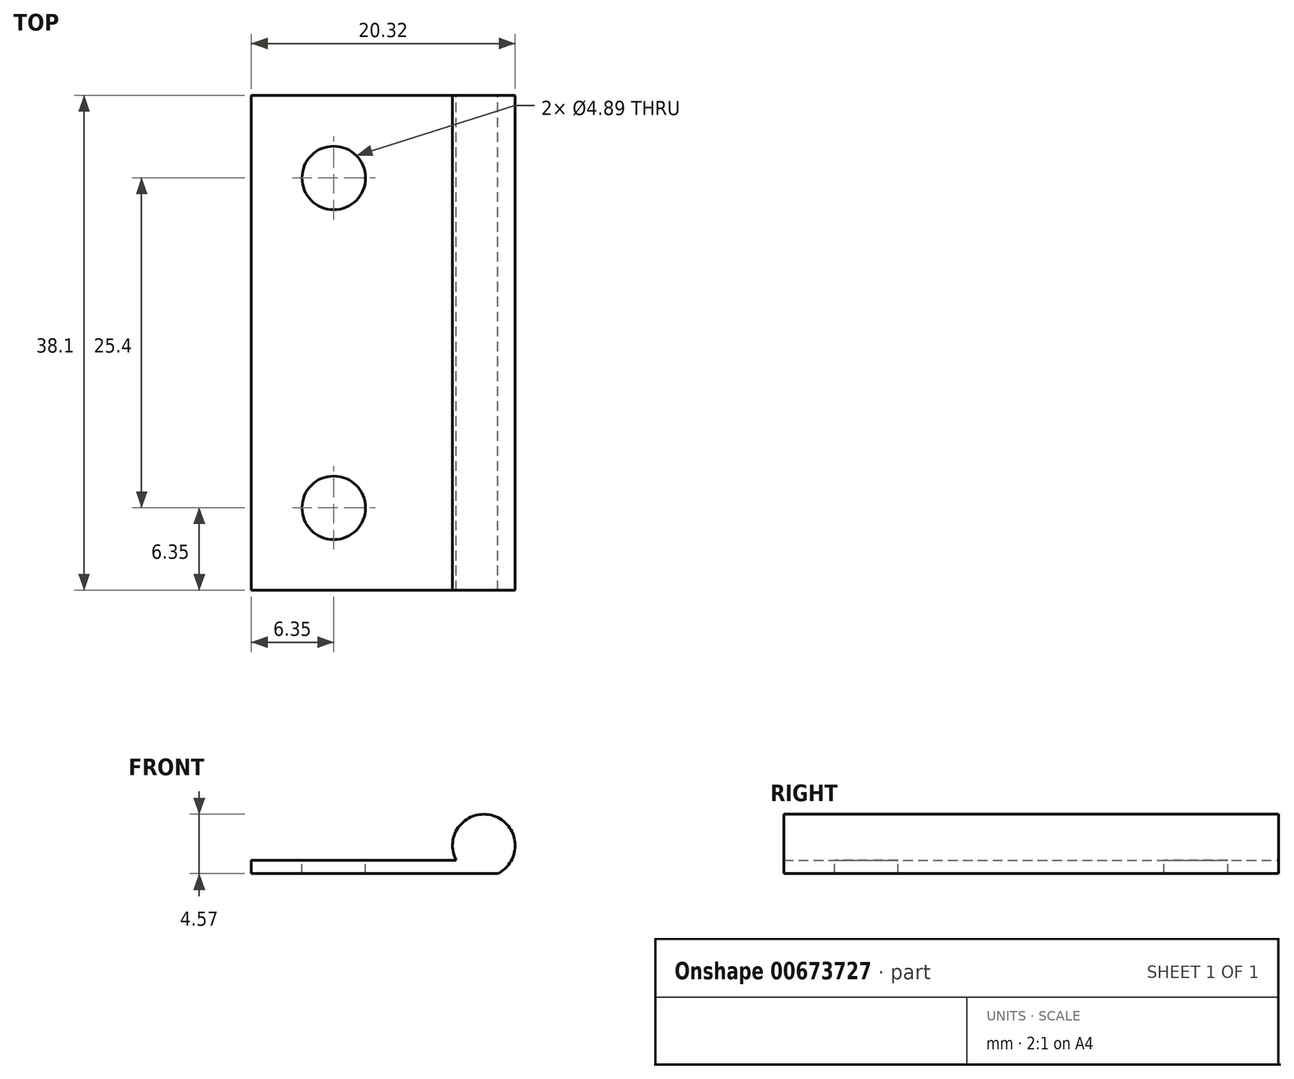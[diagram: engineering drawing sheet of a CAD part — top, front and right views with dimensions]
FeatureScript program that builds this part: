
annotation { "Feature Type Name" : "Feature", "Feature Type Description" : "" }
export const myFeature = defineFeature(function(context is Context, id is Id, definition is map)
    precondition{}
    {
        {
            var Q0;
            Q0=qCreatedBy(makeId("Front.planeOp"),FACE);
            var sketch = newSketch(context, id + "F0", { "sketchPlane" : qUnion([Q0])});
            skLineSegment(sketch, "E0.bottom", {"start": v(0, 0) * mm, "end": v(20.32, 0) * mm});
            skLineSegment(sketch, "E0.top", {"start": v(0, 1.02) * mm, "end": v(20.32, 1.02) * mm});
            skLineSegment(sketch, "E0.left", {"start": v(0, 0) * mm, "end": v(0, 1.02) * mm});
            skLineSegment(sketch, "E0.right", {"start": v(20.32, 0) * mm, "end": v(20.32, 1.02) * mm});
            skCircle(sketch, "E1", {"center": v(17.9, 2.16) * mm, "radius": 2.41 * mm});
            skLineSegment(sketch, "E2", {"start": v(20.32, 1.02) * mm, "end": v(20.32, 2.16) * mm});
            skSolve(sketch);
        }
        {
            var Q0;
            {var subQ0=sQuery(id+"F0.wireOp",EDGE,"E0.left");Q0=makeQuery(id+"F0.imprint","IMPRINT",FACE,{"disambiguationData":[TD([[makeQuery(id+"F0.imprint","IMPRINT",EDGE,{"derivedFrom":subQ0}),-1.0]])]});}
            var Q1;
            {var subQ0=sQuery(id+"F0.wireOp",EDGE,"E1");var subQ1=sQuery(id+"F0.wireOp",EDGE,"E0.bottom");var subQ2=makeQuery(id+"F0.imprint","INTERSECT",VERTEX,{"disambiguationData":[OD(0.0)],"derivedFrom":[subQ1,subQ0]});Q1=makeQuery(id+"F0.imprint","IMPRINT",FACE,{"disambiguationData":[TD([[makeQuery(id+"F0.imprint","IMPRINT",EDGE,{"disambiguationData":[TD([[subQ2,-1.0]])],"derivedFrom":subQ1}),1.0]])]});}
            var Q2;
            {var subQ0=sQuery(id+"F0.wireOp",EDGE,"E1");var subQ1=sQuery(id+"F0.wireOp",EDGE,"E0.top");var subQ2=makeQuery(id+"F0.imprint","INTERSECT",VERTEX,{"disambiguationData":[OD(0.0)],"derivedFrom":[subQ1,subQ0]});Q2=makeQuery(id+"F0.imprint","IMPRINT",FACE,{"disambiguationData":[TD([[makeQuery(id+"F0.imprint","IMPRINT",EDGE,{"disambiguationData":[TD([[subQ2,-1.0]])],"derivedFrom":subQ1}),1.0]])]});}
            extrude(context, id + "F1", {"entities" : qUnion([Q0, Q1, Q2]), "depth" : 38.1 * mm, "offsetDistance" : 25.4 * mm});
        }
        {
            var Q0;
            Q0=makeQuery(id+"F1.opExtrude","SWEPT_FACE",FACE,{"disambiguationData":[OSD([sQuery(id+"F0.wireOp",EDGE,"E0.top")])]});
            var sketch = newSketch(context, id + "F2", { "sketchPlane" : qUnion([Q0])});
            skCircle(sketch, "E3", {"center": v(6.35, -31.75) * mm, "radius": 2.44 * mm});
            skCircle(sketch, "E4", {"center": v(6.35, -6.35) * mm, "radius": 2.44 * mm});
            skLineSegment(sketch, "E5", {"start": v(6.35, -6.35) * mm, "end": v(6.35, -31.75) * mm, "construction": true});
            skPoint(sketch, "E6", {"position": v(6.35, -19.05) * mm});
            skLineSegment(sketch, "E7", {"start": v(0, -19.05) * mm, "end": v(15.78, -19.05) * mm, "construction": true});
            skSolve(sketch);
        }
        {
            var Q0;
            Q0=makeQuery(id+"F2.imprint","IMPRINT",FACE,{"disambiguationData":[TD([[makeQuery(id+"F2.imprint","IMPRINT",EDGE,{"derivedFrom":sQuery(id+"F2.wireOp",EDGE,"E4")}),1.0]])]});
            var Q1;
            Q1=makeQuery(id+"F2.imprint","IMPRINT",FACE,{"disambiguationData":[TD([[makeQuery(id+"F2.imprint","IMPRINT",EDGE,{"derivedFrom":sQuery(id+"F2.wireOp",EDGE,"E3")}),1.0]])]});
            extrude(context, id + "F3", {"entities" : qUnion([Q0, Q1]), "operationType" : NewBodyOperationType.REMOVE, "oppositeDirection" : true, "depth" : 25.4 * mm, "offsetDistance" : 25.4 * mm});
        }
    });
